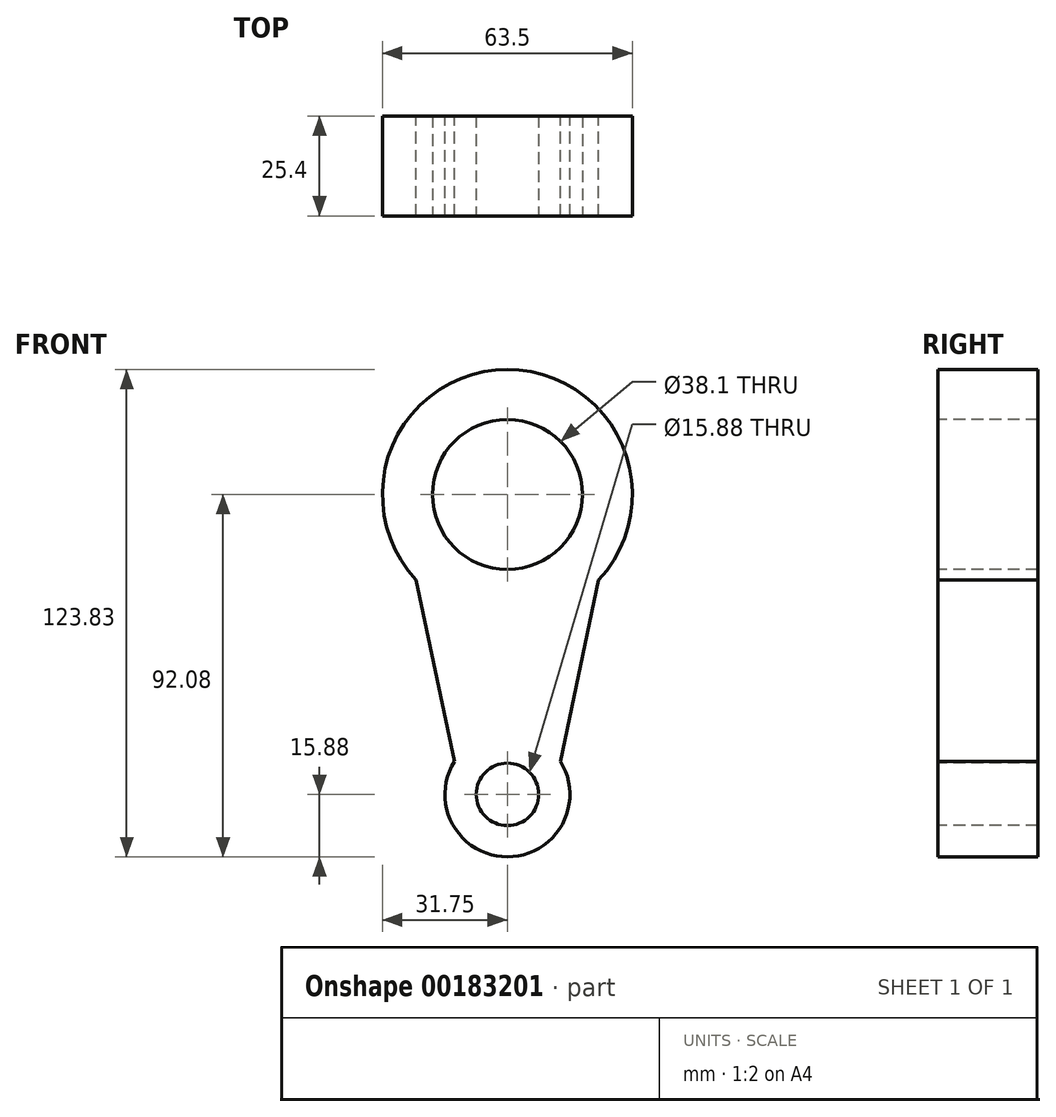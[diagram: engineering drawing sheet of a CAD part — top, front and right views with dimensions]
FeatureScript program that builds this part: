
annotation { "Feature Type Name" : "Feature", "Feature Type Description" : "" }
export const myFeature = defineFeature(function(context is Context, id is Id, definition is map)
    precondition{}
    {
        {
            var Q0;
            Q0=qCreatedBy(makeId("Front.planeOp"),FACE);
            var sketch = newSketch(context, id + "F0", { "sketchPlane" : qUnion([Q0])});
            skCircle(sketch, "E0", {"center": v(0, 0) * mm, "radius": 31.75 * mm});
            skCircle(sketch, "E1", {"center": v(0, -76.2) * mm, "radius": 15.88 * mm});
            skLineSegment(sketch, "E2", {"start": v(23.18, -21.7) * mm, "end": v(13.46, -67.78) * mm});
            skLineSegment(sketch, "E3.MirrorCS", {"start": v(-23.18, -21.7) * mm, "end": v(-13.46, -67.78) * mm});
            skSolve(sketch);
        }
        {
            var Q0;
            Q0=makeQuery(id+"F0.imprint","IMPRINT",FACE,{"disambiguationData":[TD([[makeQuery(id+"F0.imprint","IMPRINT",EDGE,{"derivedFrom":sQuery(id+"F0.wireOp",EDGE,"E0")}),1.0]])]});
            extrude(context, id + "F1", {"entities" : qUnion([Q0]), "endBound" : BoundingType.SYMMETRIC, "depth" : 25.4 * mm});
        }
        {
            var Q0;
            {var subQ0=sQuery(id+"F0.wireOp",EDGE,"E2");Q0=makeQuery(id+"F0.imprint","IMPRINT",FACE,{"disambiguationData":[TD([[makeQuery(id+"F0.imprint","IMPRINT",EDGE,{"derivedFrom":subQ0}),-1.0]])]});}
            var Q1;
            {var subQ0=sQuery(id+"F0.wireOp",EDGE,"E1");var subQ1=makeQuery(id+"F0.imprint","INTERSECT",VERTEX,{"derivedFrom":[subQ0,sQuery(id+"F0.wireOp",EDGE,"E2")]});Q1=makeQuery(id+"F0.imprint","IMPRINT",FACE,{"disambiguationData":[TD([[makeQuery(id+"F0.imprint","IMPRINT",EDGE,{"disambiguationData":[TD([[subQ1,-1.0]])],"derivedFrom":subQ0}),1.0]])]});}
            extrude(context, id + "F2", {"entities" : qUnion([Q0, Q1]), "operationType" : NewBodyOperationType.ADD, "endBound" : BoundingType.SYMMETRIC, "depth" : 25.4 * mm});
        }
        {
            var Q0;
            {var subQ0=sQuery(id+"F0.wireOp",EDGE,"E0");Q0=makeQuery(id+"F2.boolean.opBoolean","MERGE",FACE,{"derivedFrom":[makeQuery(id+"F1.opExtrude","CAP_FACE",FACE,{"disambiguationData":[OSD([subQ0])],"isStart":false}),makeQuery(id+"F2.opExtrude","CAP_FACE",FACE,{"disambiguationData":[OSD([subQ0,sQuery(id+"F0.wireOp",EDGE,"E1"),sQuery(id+"F0.wireOp",EDGE,"E2"),sQuery(id+"F0.wireOp",EDGE,"E3.MirrorCS")])],"isStart":false})]});}
            var sketch = newSketch(context, id + "F3", { "sketchPlane" : qUnion([Q0])});
            skCircle(sketch, "E4", {"center": v(0, 0) * mm, "radius": 19.05 * mm});
            skSolve(sketch);
        }
        {
            var Q0;
            Q0 = qSketchRegion(id + "F3", true);
            extrude(context, id + "F4", {"entities" : qUnion([Q0]), "operationType" : NewBodyOperationType.REMOVE, "endBound" : BoundingType.THROUGH_ALL, "oppositeDirection" : true, "depth" : 25.4 * mm});
        }
        {
            var Q0;
            {var subQ0=sQuery(id+"F0.wireOp",EDGE,"E0");Q0=makeQuery(id+"F2.boolean.opBoolean","MERGE",FACE,{"derivedFrom":[makeQuery(id+"F1.opExtrude","CAP_FACE",FACE,{"disambiguationData":[OSD([subQ0])],"isStart":false}),makeQuery(id+"F2.opExtrude","CAP_FACE",FACE,{"disambiguationData":[OSD([subQ0,sQuery(id+"F0.wireOp",EDGE,"E1"),sQuery(id+"F0.wireOp",EDGE,"E2"),sQuery(id+"F0.wireOp",EDGE,"E3.MirrorCS")])],"isStart":false})]});}
            var sketch = newSketch(context, id + "F5", { "sketchPlane" : qUnion([Q0])});
            skCircle(sketch, "E5", {"center": v(0, -76.2) * mm, "radius": 7.94 * mm});
            skSolve(sketch);
        }
        {
            var Q0;
            Q0 = qSketchRegion(id + "F5", true);
            extrude(context, id + "F6", {"entities" : qUnion([Q0]), "operationType" : NewBodyOperationType.REMOVE, "endBound" : BoundingType.THROUGH_ALL, "oppositeDirection" : true, "depth" : 25.4 * mm});
        }
    });
